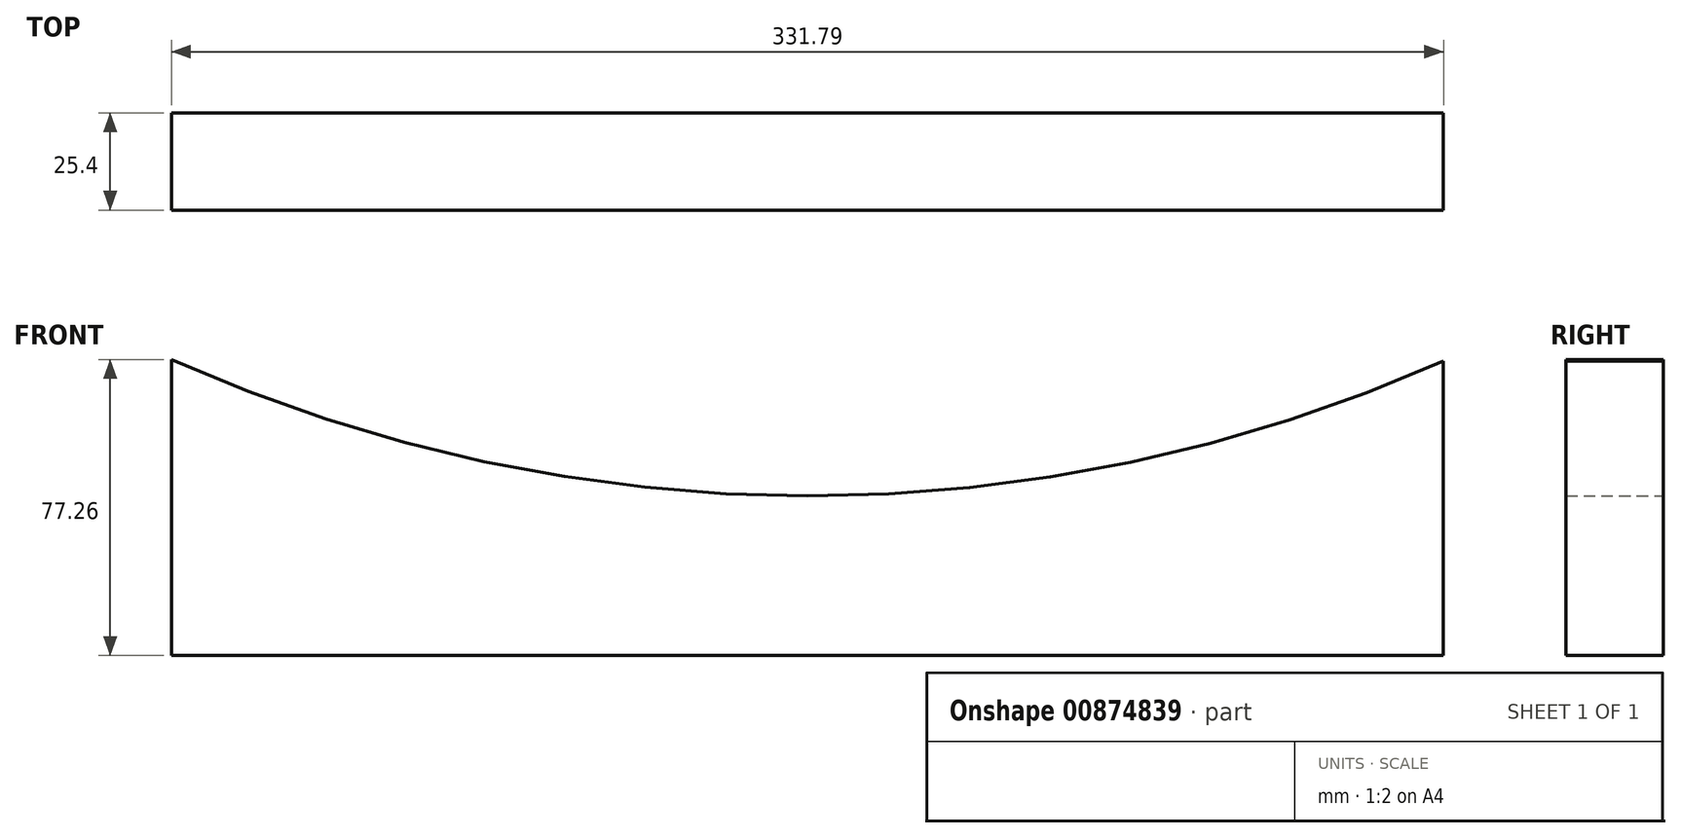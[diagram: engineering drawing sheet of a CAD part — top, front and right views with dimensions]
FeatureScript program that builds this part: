
annotation { "Feature Type Name" : "Feature", "Feature Type Description" : "" }
export const myFeature = defineFeature(function(context is Context, id is Id, definition is map)
    precondition{}
    {
        {
            var Q0;
            Q0=qCreatedBy(makeId("Front.planeOp"),FACE);
            var sketch = newSketch(context, id + "F0", { "sketchPlane" : qUnion([Q0])});
            skLineSegment(sketch, "E0", {"start": v(-67.86, 49.2) * mm, "end": v(-67.86, -28.07) * mm});
            skLineSegment(sketch, "E1", {"start": v(-67.86, -28.07) * mm, "end": v(263.93, -28.07) * mm});
            skLineSegment(sketch, "E2", {"start": v(263.93, -28.07) * mm, "end": v(263.93, 48.82) * mm});
            skArc(sketch, "E3", {"start": v(-67.86, 49.2) * mm, "mid": v(98, 13.6) * mm, "end": v(263.93, 48.82) * mm});
            skSolve(sketch);
        }
        {
            var Q0;
            Q0 = qSketchRegion(id + "F0", true);
            extrude(context, id + "F1", {"entities" : qUnion([Q0]), "depth" : 25.4 * mm, "offsetDistance" : 25.4 * mm});
        }
    });
